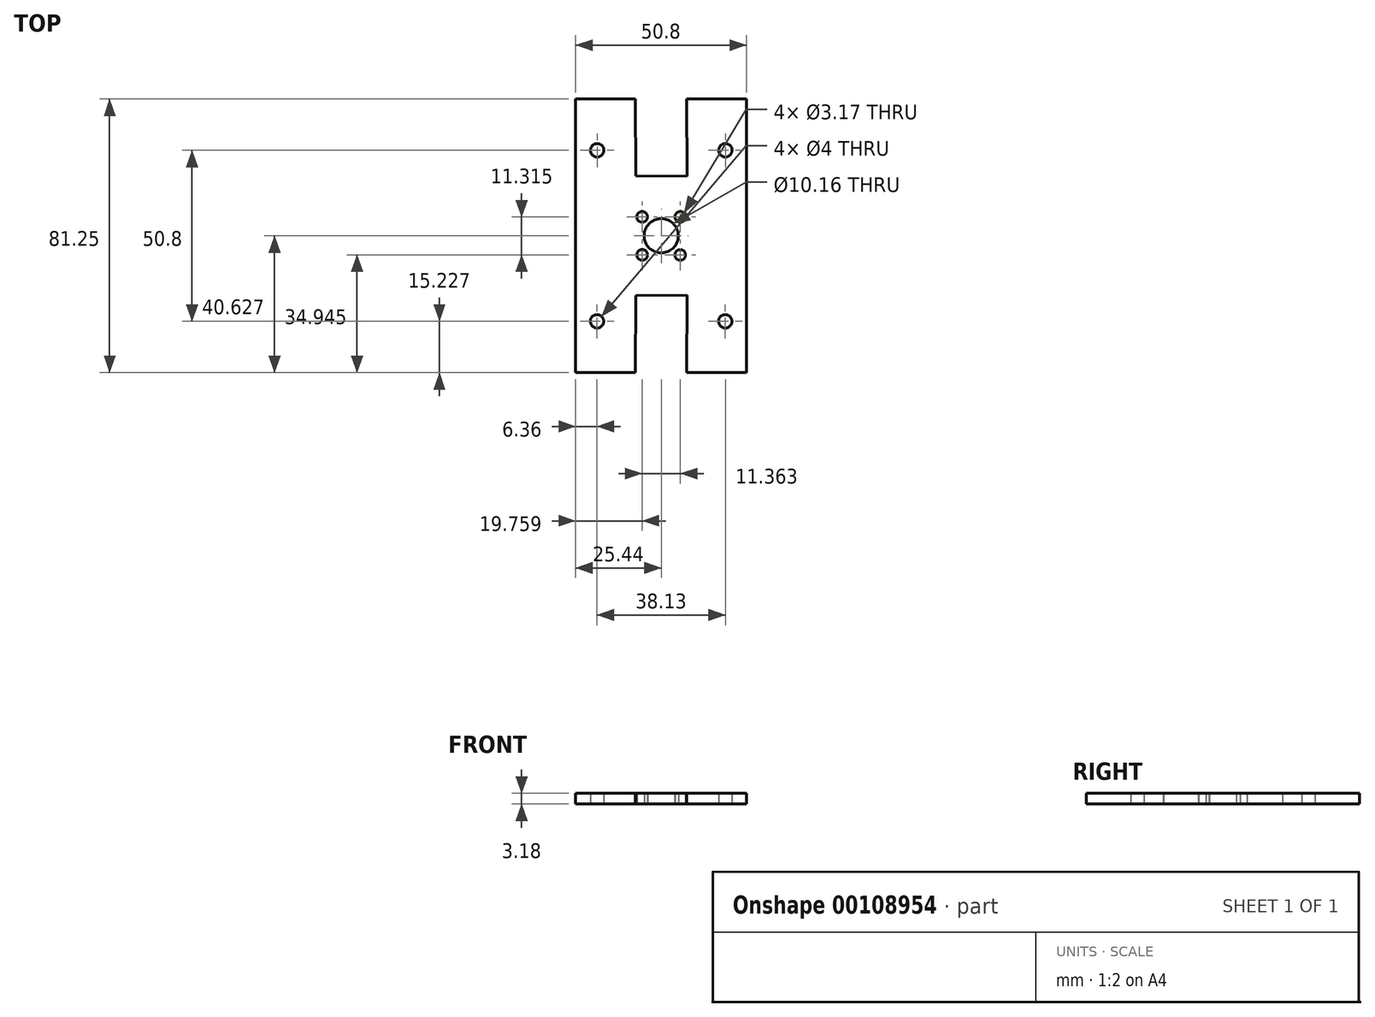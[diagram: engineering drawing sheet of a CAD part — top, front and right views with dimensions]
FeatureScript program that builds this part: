
annotation { "Feature Type Name" : "Feature", "Feature Type Description" : "" }
export const myFeature = defineFeature(function(context is Context, id is Id, definition is map)
    precondition{}
    {
        {
            var Q0;
            Q0=qCreatedBy(makeId("Top.planeOp"),FACE);
            var sketch = newSketch(context, id + "F0", { "sketchPlane" : qUnion([Q0])});
            skLineSegment(sketch, "E0.bottom", {"start": v(-25.44, 25.5) * mm, "end": v(-7.64, 25.5) * mm});
            skCircle(sketch, "E1", {"center": v(0, 66.13) * mm, "radius": 5.08 * mm});
            skCircle(sketch, "E2", {"center": v(-5.68, 71.76) * mm, "radius": 1.59 * mm});
            skCircle(sketch, "E3", {"center": v(-5.66, 60.47) * mm, "radius": 1.59 * mm});
            skCircle(sketch, "E4", {"center": v(5.68, 71.76) * mm, "radius": 1.59 * mm});
            skCircle(sketch, "E5", {"center": v(5.63, 60.45) * mm, "radius": 1.59 * mm});
            skLineSegment(sketch, "E6.bottom", {"start": v(-7.62, 48.36) * mm, "end": v(7.62, 48.48) * mm});
            skLineSegment(sketch, "E6.left", {"start": v(-7.62, 48.36) * mm, "end": v(-7.64, 25.5) * mm});
            skLineSegment(sketch, "E6.right", {"start": v(7.62, 48.48) * mm, "end": v(7.6, 25.5) * mm});
            skCircle(sketch, "E7", {"center": v(19.02, 40.73) * mm, "radius": 2 * mm});
            skCircle(sketch, "E8", {"center": v(-19.08, 40.73) * mm, "radius": 2 * mm});
            skPoint(sketch, "E9", {"position": v(0, 48.42) * mm});
            skLineSegment(sketch, "E10.trimOffspring", {"start": v(7.6, 25.5) * mm, "end": v(25.36, 25.5) * mm});
            skLineSegment(sketch, "E11.MirrorCS", {"start": v(-7.62, 83.9) * mm, "end": v(7.62, 83.77) * mm});
            skLineSegment(sketch, "E12.MirrorCS", {"start": v(7.62, 83.77) * mm, "end": v(7.6, 106.75) * mm});
            skLineSegment(sketch, "E13.MirrorCS", {"start": v(7.6, 106.75) * mm, "end": v(25.36, 106.75) * mm});
            skLineSegment(sketch, "E14.MirrorCS", {"start": v(-25.44, 106.75) * mm, "end": v(-7.64, 106.75) * mm});
            skCircle(sketch, "E15.MirrorC", {"center": v(-19.05, 91.53) * mm, "radius": 2 * mm});
            skCircle(sketch, "E16.MirrorC", {"center": v(19.05, 91.53) * mm, "radius": 2 * mm});
            skLineSegment(sketch, "E17.MirrorCS", {"start": v(-7.62, 83.9) * mm, "end": v(-7.64, 106.75) * mm});
            skPoint(sketch, "E18.MirrorCS.start.orphan", {"position": v(25.36, 106.75) * mm});
            skLineSegment(sketch, "E19", {"start": v(-25.44, 106.75) * mm, "end": v(-25.44, 25.5) * mm});
            skLineSegment(sketch, "E20", {"start": v(25.36, 25.5) * mm, "end": v(25.36, 106.75) * mm});
            skSolve(sketch);
        }
        {
            var Q0;
            Q0=makeQuery(id+"F0.imprint","IMPRINT",FACE,{"disambiguationData":[TD([[makeQuery(id+"F0.imprint","IMPRINT",EDGE,{"derivedFrom":sQuery(id+"F0.wireOp",EDGE,"2006bb52-2d54-4f0e-ba05-1ae574e5513b")}),1.0]])]});
            var Q1;
            Q1=makeQuery(id+"F0.imprint","IMPRINT",FACE,{"disambiguationData":[TD([[makeQuery(id+"F0.imprint","IMPRINT",EDGE,{"derivedFrom":sQuery(id+"F0.wireOp",EDGE,"E0.top")}),-1.0]])]});
            var Q2;
            Q2=makeQuery(id+"F0.imprint","IMPRINT",FACE,{"disambiguationData":[TD([[makeQuery(id+"F0.imprint","IMPRINT",EDGE,{"derivedFrom":sQuery(id+"F0.wireOp",EDGE,"E0.bottom")}),1.0]])]});
            extrude(context, id + "F1", {"entities" : qUnion([Q0, Q1, Q2]), "depth" : 3.17 * mm});
        }
    });
